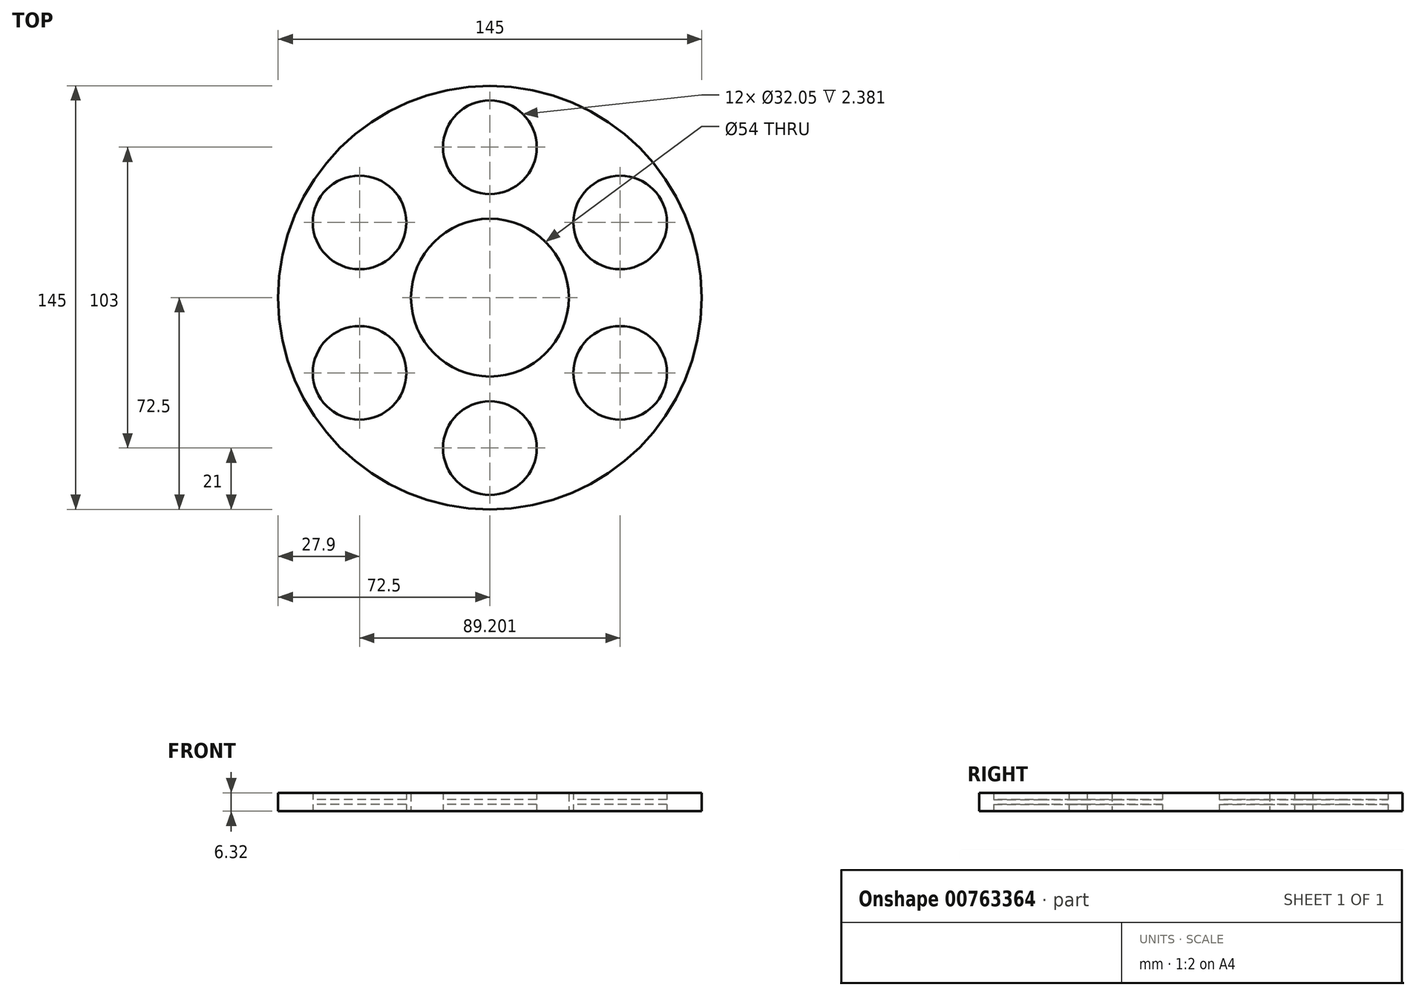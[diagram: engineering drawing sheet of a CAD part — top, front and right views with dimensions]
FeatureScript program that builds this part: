
annotation { "Feature Type Name" : "Feature", "Feature Type Description" : "" }
export const myFeature = defineFeature(function(context is Context, id is Id, definition is map)
    precondition{}
    {
        {
            var Q0;
            Q0=qCreatedBy(makeId("Top.planeOp"),FACE);
            var sketch = newSketch(context, id + "F0", { "sketchPlane" : qUnion([Q0])});
            skCircle(sketch, "E0", {"center": v(0, 0) * mm, "radius": 72.5 * mm});
            skLineSegment(sketch, "E1", {"start": v(0, 72.5) * mm, "end": v(0, 67.5) * mm});
            skLineSegment(sketch, "E2", {"start": v(0, 67.5) * mm, "end": v(0, 51.5) * mm});
            skCircle(sketch, "E3", {"center": v(0, 51.5) * mm, "radius": 16.02 * mm});
            skCircle(sketch, "E4.1.0", {"center": v(-44.6, 25.75) * mm, "radius": 16.02 * mm});
            skCircle(sketch, "E4.2.0", {"center": v(-44.6, -25.75) * mm, "radius": 16.02 * mm});
            skCircle(sketch, "E4.3.0", {"center": v(0, -51.5) * mm, "radius": 16.02 * mm});
            skCircle(sketch, "E4.4.0", {"center": v(44.6, -25.75) * mm, "radius": 16.02 * mm});
            skCircle(sketch, "E4.5.0", {"center": v(44.6, 25.75) * mm, "radius": 16.02 * mm});
            skCircle(sketch, "E5", {"center": v(0, 0) * mm, "radius": 11.12 * mm});
            skCircle(sketch, "E6", {"center": v(0, 0) * mm, "radius": 27 * mm});
            skCircle(sketch, "E7", {"center": v(0, 0) * mm, "radius": 14.5 * mm});
            skSolve(sketch);
        }
        {
            var Q0;
            Q0 = qSketchRegion(id + "F0", true);
            extrude(context, id + "F1", {"entities" : qUnion([Q0]), "depth" : 4.76 * mm, "offsetDistance" : 25 * mm, "symmetric" : true});
        }
        {
            var Q0;
            Q0=makeQuery(id+"F0.imprint","IMPRINT",FACE,{"disambiguationData":[TD([[makeQuery(id+"F0.imprint","IMPRINT",EDGE,{"derivedFrom":sQuery(id+"F0.wireOp",EDGE,"E4.1.0")}),1.0]])]});
            var Q1;
            Q1=makeQuery(id+"F0.imprint","IMPRINT",FACE,{"disambiguationData":[TD([[makeQuery(id+"F0.imprint","IMPRINT",EDGE,{"derivedFrom":sQuery(id+"F0.wireOp",EDGE,"E3")}),1.0]])]});
            var Q2;
            Q2=makeQuery(id+"F0.imprint","IMPRINT",FACE,{"disambiguationData":[TD([[makeQuery(id+"F0.imprint","IMPRINT",EDGE,{"derivedFrom":sQuery(id+"F0.wireOp",EDGE,"E4.5.0")}),1.0]])]});
            var Q3;
            Q3=makeQuery(id+"F0.imprint","IMPRINT",FACE,{"disambiguationData":[TD([[makeQuery(id+"F0.imprint","IMPRINT",EDGE,{"derivedFrom":sQuery(id+"F0.wireOp",EDGE,"E4.4.0")}),1.0]])]});
            var Q4;
            Q4=makeQuery(id+"F0.imprint","IMPRINT",FACE,{"disambiguationData":[TD([[makeQuery(id+"F0.imprint","IMPRINT",EDGE,{"derivedFrom":sQuery(id+"F0.wireOp",EDGE,"E4.3.0")}),1.0]])]});
            var Q5;
            Q5=makeQuery(id+"F0.imprint","IMPRINT",FACE,{"disambiguationData":[TD([[makeQuery(id+"F0.imprint","IMPRINT",EDGE,{"derivedFrom":sQuery(id+"F0.wireOp",EDGE,"E4.2.0")}),1.0]])]});
            var Q6;
            Q6=makeQuery(id+"F1.opExtrude","CAP_FACE",FACE,{"disambiguationData":[OSD([sQuery(id+"F0.wireOp",EDGE,"E0"),sQuery(id+"F0.wireOp",EDGE,"E3"),sQuery(id+"F0.wireOp",EDGE,"E4.1.0"),sQuery(id+"F0.wireOp",EDGE,"E4.2.0"),sQuery(id+"F0.wireOp",EDGE,"E4.3.0"),sQuery(id+"F0.wireOp",EDGE,"E4.4.0"),sQuery(id+"F0.wireOp",EDGE,"E4.5.0"),sQuery(id+"F0.wireOp",EDGE,"E5")])],"isStart":false});
            var Q7;
            Q7=makeQuery(id+"F1.opExtrude","CAP_FACE",FACE,{"disambiguationData":[OSD([sQuery(id+"F0.wireOp",EDGE,"E0"),sQuery(id+"F0.wireOp",EDGE,"E3"),sQuery(id+"F0.wireOp",EDGE,"E4.1.0"),sQuery(id+"F0.wireOp",EDGE,"E4.2.0"),sQuery(id+"F0.wireOp",EDGE,"E4.3.0"),sQuery(id+"F0.wireOp",EDGE,"E4.4.0"),sQuery(id+"F0.wireOp",EDGE,"E4.5.0"),sQuery(id+"F0.wireOp",EDGE,"E5")])],"isStart":true});
            extrude(context, id + "F2", {"entities" : qUnion([Q0, Q1, Q2, Q3, Q4, Q5, Q6, Q7]), "operationType" : NewBodyOperationType.ADD, "depth" : 1.56 * mm, "offsetDistance" : 25 * mm});
        }
    });
